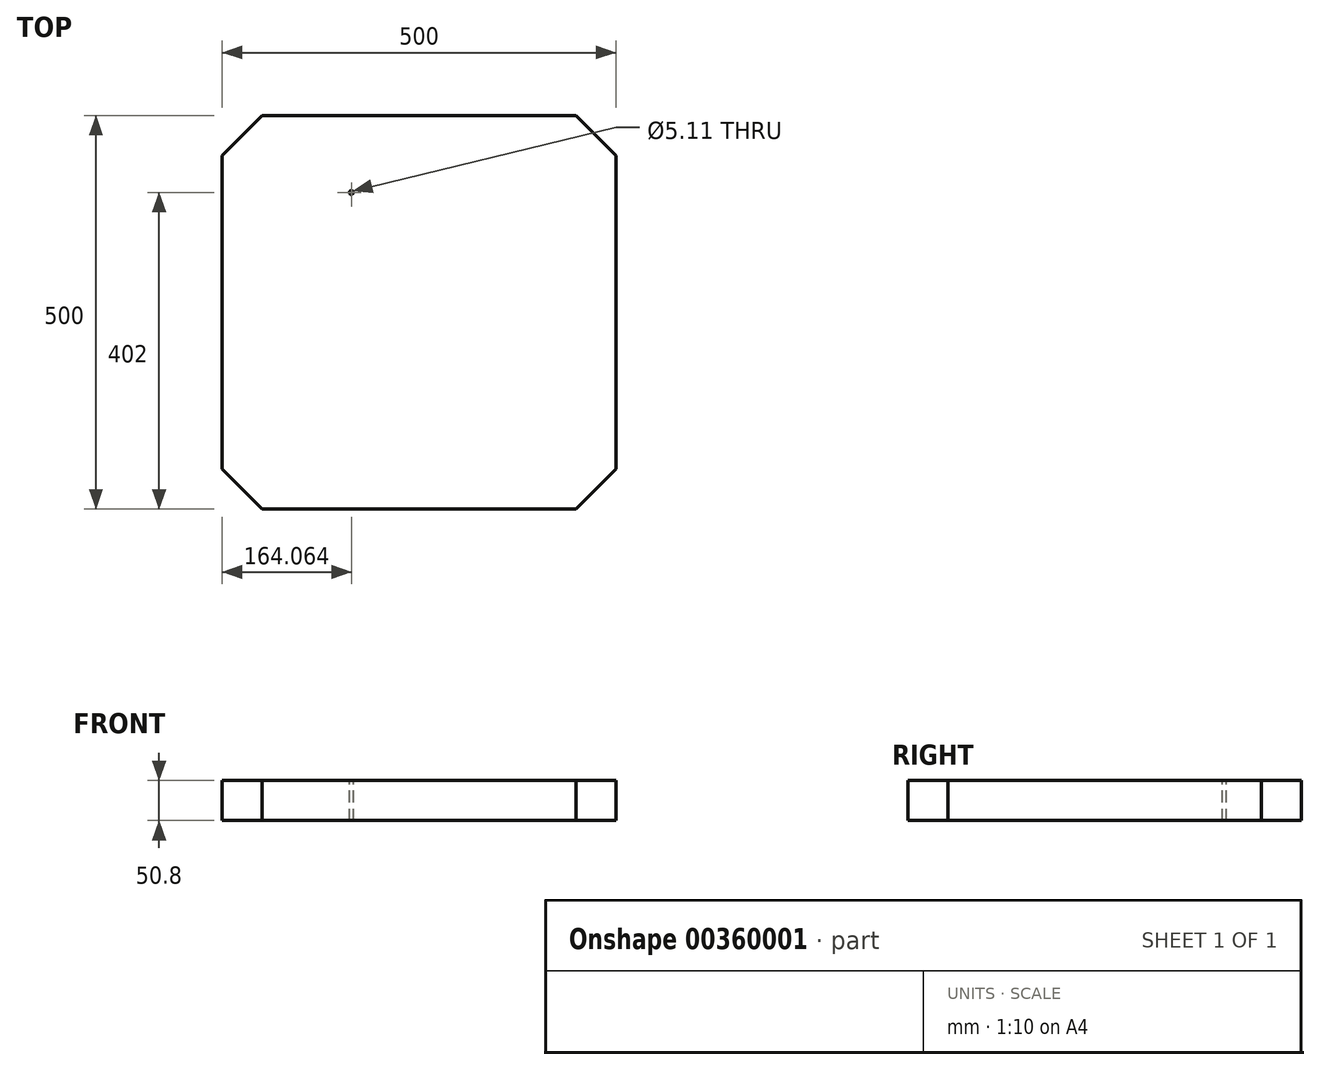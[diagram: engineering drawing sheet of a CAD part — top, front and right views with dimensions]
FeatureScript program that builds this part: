
annotation { "Feature Type Name" : "Feature", "Feature Type Description" : "" }
export const myFeature = defineFeature(function(context is Context, id is Id, definition is map)
    precondition{}
    {
        {
            var Q0;
            Q0=qCreatedBy(makeId("Top.planeOp"),FACE);
            var sketch = newSketch(context, id + "F0", { "sketchPlane" : qUnion([Q0])});
            skLineSegment(sketch, "E0.top", {"start": v(-250, -250) * mm, "end": v(250, -250) * mm});
            skLineSegment(sketch, "E0.right", {"start": v(250, 250) * mm, "end": v(250, -250) * mm});
            skPoint(sketch, "E0.middle", {"position": v(0, 0) * mm});
            skLineSegment(sketch, "E1", {"start": v(-250, 250) * mm, "end": v(250, 250) * mm});
            skLineSegment(sketch, "E2", {"start": v(-250, 250) * mm, "end": v(-250, -250) * mm});
            skSolve(sketch);
        }
        {
            var Q0;
            Q0 = qSketchRegion(id + "F0", true);
            extrude(context, id + "F1", {"entities" : qUnion([Q0]), "depth" : 50.8 * mm});
        }
        {
            var Q0;
            Q0=makeQuery(id+"F1.opExtrude","CAP_FACE",FACE,{"disambiguationData":[OSD([sQuery(id+"F0.wireOp",EDGE,"E0.top"),sQuery(id+"F0.wireOp",EDGE,"E0.right"),sQuery(id+"F0.wireOp",EDGE,"ccOverqi-Q5QR-f9xp-5AkG-c4gMYnRPv0PY"),sQuery(id+"F0.wireOp",EDGE,"E1"),sQuery(id+"F0.wireOp",EDGE,"E2")])],"isStart":false});
            var sketch = newSketch(context, id + "F2", { "sketchPlane" : qUnion([Q0])});
            skPoint(sketch, "E3", {"position": v(-85.94, 152) * mm});
            skPoint(sketch, "E4", {"position": v(81.05, 149.4) * mm});
            skPoint(sketch, "E5", {"position": v(-92.07, -72.6) * mm});
            skPoint(sketch, "E6", {"position": v(79.54, -58.32) * mm});
            skSolve(sketch);
        }
        {
            var Q0;
            Q0=sQuery(id+"F2.wireOp",VERTEX,"E3");
            var Q1;
            Q1=makeQuery(id+"F1.opExtrude","SWEPT_BODY",BODY,{"disambiguationData":[OSD([sQuery(id+"F0.wireOp",EDGE,"E0.top"),sQuery(id+"F0.wireOp",EDGE,"E0.right"),sQuery(id+"F0.wireOp",EDGE,"ccOverqi-Q5QR-f9xp-5AkG-c4gMYnRPv0PY"),sQuery(id+"F0.wireOp",EDGE,"E1"),sQuery(id+"F0.wireOp",EDGE,"E2")])]});
            hole(context, id + "F3", {"style" : HoleStyle.SIMPLE, "endStyle" : HoleEndStyle.THROUGH, "standardTappedOrClearance" : lookupTablePath({ "standard" : "ANSI", "engagement" : "75%", "pitch" : "20 tpi", "size" : "1/4", "type" : "Tapped" }), "standardBlindInLast" : lookupTablePath({ "standard" : "ANSI", "engagement" : "75%", "pitch" : "20 tpi", "size" : "1/4", "type" : "Tapped" }), "holeDiameter" : 5.1 * mm, "showTappedDepth" : true, "isTappedThrough" : true, "tappedDepth" : 12.7 * mm, "tapClearance" : 3, "locations" : qUnion([Q0]), "scope" : qUnion([Q1]), "majorDiameter" : 6.35 * mm});
        }
        {
            var Q0;
            Q0=makeQuery(id+"F1.opExtrude","SWEPT_EDGE",EDGE,{"disambiguationData":[OSD([sQuery(id+"F0.wireOp",EDGE,"E1"),sQuery(id+"F0.wireOp",EDGE,"E2")])]});
            var Q1;
            Q1=makeQuery(id+"F1.opExtrude","SWEPT_EDGE",EDGE,{"disambiguationData":[OSD([sQuery(id+"F0.wireOp",EDGE,"E0.top"),sQuery(id+"F0.wireOp",EDGE,"E2")])]});
            var Q2;
            Q2=makeQuery(id+"F1.opExtrude","SWEPT_EDGE",EDGE,{"disambiguationData":[OSD([sQuery(id+"F0.wireOp",EDGE,"E0.top"),sQuery(id+"F0.wireOp",EDGE,"E0.right")])]});
            var Q3;
            Q3=makeQuery(id+"F1.opExtrude","SWEPT_EDGE",EDGE,{"disambiguationData":[OSD([sQuery(id+"F0.wireOp",EDGE,"E0.right"),sQuery(id+"F0.wireOp",EDGE,"E1")])]});
            chamfer(context, id + "F4", {"entities" : qUnion([Q0, Q1, Q2, Q3]), "width" : 50.8 * mm, "tangentPropagation" : true});
        }
    });
